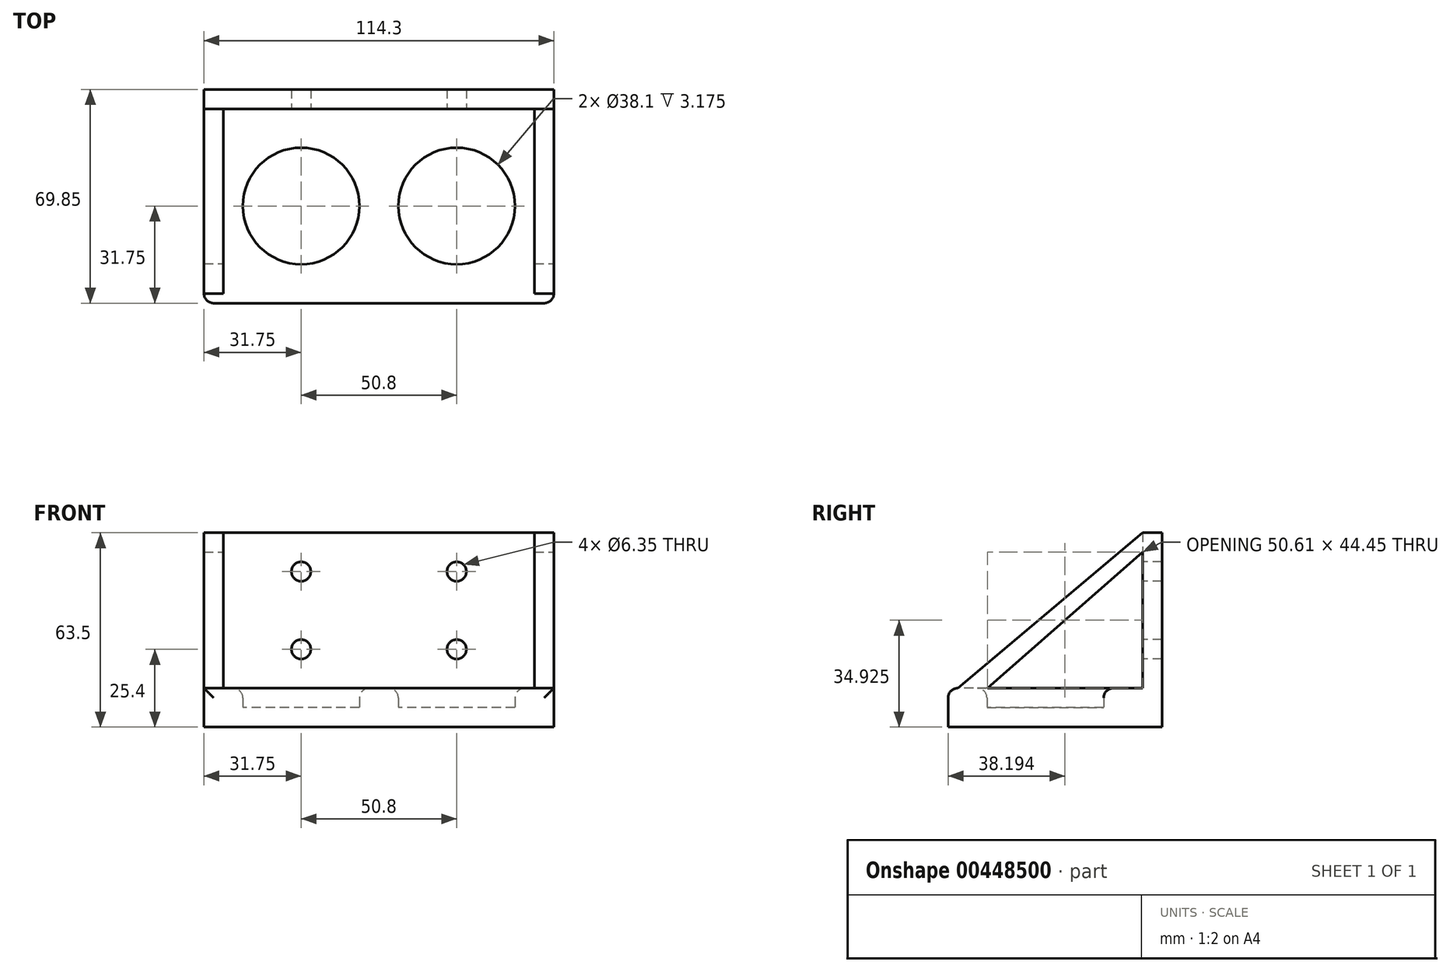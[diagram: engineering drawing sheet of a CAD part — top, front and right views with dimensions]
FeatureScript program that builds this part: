
annotation { "Feature Type Name" : "Feature", "Feature Type Description" : "" }
export const myFeature = defineFeature(function(context is Context, id is Id, definition is map)
    precondition{}
    {
        {
            var Q0;
            Q0=qCreatedBy(makeId("Top.planeOp"),FACE);
            var sketch = newSketch(context, id + "F0", { "sketchPlane" : qUnion([Q0])});
            skLineSegment(sketch, "E0.bottom", {"start": v(57.15, -31.75) * mm, "end": v(-57.15, -31.75) * mm});
            skLineSegment(sketch, "E0.top", {"start": v(57.15, 31.75) * mm, "end": v(-57.15, 31.75) * mm});
            skLineSegment(sketch, "E0.left", {"start": v(57.15, -31.75) * mm, "end": v(57.15, 31.75) * mm});
            skLineSegment(sketch, "E0.right", {"start": v(-57.15, -31.75) * mm, "end": v(-57.15, 31.75) * mm});
            skPoint(sketch, "E0.middle", {"position": v(0, 0) * mm});
            skCircle(sketch, "E1", {"center": v(-25.4, 0) * mm, "radius": 19.05 * mm});
            skCircle(sketch, "E2", {"center": v(25.4, 0) * mm, "radius": 19.05 * mm});
            skSolve(sketch);
        }
        {
            var Q0;
            Q0=makeQuery(id+"F0.imprint","IMPRINT",FACE,{"disambiguationData":[TD([[makeQuery(id+"F0.imprint","IMPRINT",EDGE,{"derivedFrom":sQuery(id+"F0.wireOp",EDGE,"E0.bottom")}),-1.0]])]});
            extrude(context, id + "F1", {"entities" : qUnion([Q0]), "depth" : 12.7 * mm});
        }
        {
            var Q0;
            Q0=makeQuery(id+"F0.imprint","IMPRINT",FACE,{"disambiguationData":[TD([[makeQuery(id+"F0.imprint","IMPRINT",EDGE,{"derivedFrom":sQuery(id+"F0.wireOp",EDGE,"E1")}),1.0]])]});
            var Q1;
            Q1=makeQuery(id+"F0.imprint","IMPRINT",FACE,{"disambiguationData":[TD([[makeQuery(id+"F0.imprint","IMPRINT",EDGE,{"derivedFrom":sQuery(id+"F0.wireOp",EDGE,"E2")}),1.0]])]});
            extrude(context, id + "F2", {"entities" : qUnion([Q0, Q1]), "operationType" : NewBodyOperationType.ADD, "depth" : 6.35 * mm});
        }
        {
            var Q0;
            Q0=makeQuery(id+"F1.opExtrude","CAP_FACE",FACE,{"disambiguationData":[OSD([sQuery(id+"F0.wireOp",EDGE,"E0.bottom"),sQuery(id+"F0.wireOp",EDGE,"E0.top"),sQuery(id+"F0.wireOp",EDGE,"E0.left"),sQuery(id+"F0.wireOp",EDGE,"E0.right"),sQuery(id+"F0.wireOp",EDGE,"E1"),sQuery(id+"F0.wireOp",EDGE,"E2")])],"isStart":false});
            var sketch = newSketch(context, id + "F3", { "sketchPlane" : qUnion([Q0])});
            skLineSegment(sketch, "E3", {"start": v(0, 31.75) * mm, "end": v(0, -28.58) * mm, "construction": true});
            skLineSegment(sketch, "E4.bottom", {"start": v(-57.15, 31.75) * mm, "end": v(-50.8, 31.75) * mm});
            skLineSegment(sketch, "E4.top", {"start": v(-57.15, -28.57) * mm, "end": v(-50.8, -28.57) * mm});
            skLineSegment(sketch, "E4.left", {"start": v(-57.15, 31.75) * mm, "end": v(-57.15, -28.58) * mm});
            skLineSegment(sketch, "E4.right", {"start": v(-50.8, 31.75) * mm, "end": v(-50.8, -28.57) * mm});
            skLineSegment(sketch, "E5.MirrorCS", {"start": v(50.8, 31.75) * mm, "end": v(50.8, -28.57) * mm});
            skLineSegment(sketch, "E6.MirrorCS", {"start": v(57.15, 31.75) * mm, "end": v(50.8, 31.75) * mm});
            skLineSegment(sketch, "E7.MirrorCS", {"start": v(57.15, -28.57) * mm, "end": v(50.8, -28.57) * mm});
            skLineSegment(sketch, "E8.MirrorCS", {"start": v(57.15, 31.75) * mm, "end": v(57.15, -28.58) * mm});
            skSolve(sketch);
        }
        {
            var Q0;
            Q0=makeQuery(id+"F3.imprint","IMPRINT",FACE,{"disambiguationData":[TD([[makeQuery(id+"F3.imprint","IMPRINT",EDGE,{"derivedFrom":sQuery(id+"F3.wireOp",EDGE,"E4.bottom")}),1.0]])]});
            var Q1;
            Q1=makeQuery(id+"F3.imprint","IMPRINT",FACE,{"disambiguationData":[TD([[makeQuery(id+"F3.imprint","IMPRINT",EDGE,{"derivedFrom":sQuery(id+"F3.wireOp",EDGE,"E5.MirrorCS")}),1.0]])]});
            extrude(context, id + "F4", {"entities" : qUnion([Q0, Q1]), "operationType" : NewBodyOperationType.ADD, "depth" : 50.8 * mm});
        }
        {
            var Q0;
            Q0=makeQuery(id+"F4.boolean.opBoolean","MERGE",FACE,{"derivedFrom":[makeQuery(id+"F1.opExtrude","SWEPT_FACE",FACE,{"disambiguationData":[OSD([sQuery(id+"F0.wireOp",EDGE,"E0.right")])]}),makeQuery(id+"F4.opExtrude","SWEPT_FACE",FACE,{"disambiguationData":[OSD([sQuery(id+"F3.wireOp",EDGE,"E4.left")])]})]});
            var sketch = newSketch(context, id + "F5", { "sketchPlane" : qUnion([Q0])});
            skLineSegment(sketch, "E9.0", {"start": v(-31.75, 12.7) * mm, "end": v(28.57, 12.7) * mm, "construction": true});
            skLineSegment(sketch, "E10", {"start": v(-31.75, 63.5) * mm, "end": v(28.58, 12.7) * mm});
            skSolve(sketch);
        }
        {
            var Q0;
            Q0=makeQuery(id+"F5.imprint","IMPRINT",FACE,{"disambiguationData":[TD([[makeQuery(id+"F5.imprint","IMPRINT",EDGE,{"derivedFrom":sQuery(id+"F5.wireOp",EDGE,"E10")}),1.0]])]});
            extrude(context, id + "F6", {"entities" : qUnion([Q0]), "operationType" : NewBodyOperationType.REMOVE, "endBound" : BoundingType.THROUGH_ALL, "oppositeDirection" : true, "depth" : 25.4 * mm});
        }
        {
            var Q0;
            Q0=makeQuery(id+"F4.boolean.opBoolean","MERGE",FACE,{"derivedFrom":[makeQuery(id+"F1.opExtrude","SWEPT_FACE",FACE,{"disambiguationData":[OSD([sQuery(id+"F0.wireOp",EDGE,"E0.top")])]}),makeQuery(id+"F4.opExtrude","SWEPT_FACE",FACE,{"disambiguationData":[OSD([sQuery(id+"F3.wireOp",EDGE,"E4.bottom")])]}),makeQuery(id+"F4.opExtrude","SWEPT_FACE",FACE,{"disambiguationData":[OSD([sQuery(id+"F3.wireOp",EDGE,"E6.MirrorCS")])]})]});
            var sketch = newSketch(context, id + "F7", { "sketchPlane" : qUnion([Q0])});
            skLineSegment(sketch, "E11.0", {"start": v(-50.8, 63.5) * mm, "end": v(-50.8, 12.7) * mm});
            skLineSegment(sketch, "E12.0", {"start": v(-50.8, 12.7) * mm, "end": v(50.8, 12.7) * mm});
            skLineSegment(sketch, "E13.0", {"start": v(50.8, 63.5) * mm, "end": v(50.8, 12.7) * mm});
            skLineSegment(sketch, "E14", {"start": v(-50.8, 63.5) * mm, "end": v(50.8, 63.5) * mm});
            skLineSegment(sketch, "E15", {"start": v(-50.8, 63.5) * mm, "end": v(50.8, 12.7) * mm, "construction": true});
            skLineSegment(sketch, "E16", {"start": v(50.8, 63.5) * mm, "end": v(-50.8, 12.7) * mm, "construction": true});
            skLineSegment(sketch, "E17", {"start": v(-50.8, 38.1) * mm, "end": v(50.8, 38.1) * mm, "construction": true});
            skLineSegment(sketch, "E18", {"start": v(50.8, 38.1) * mm, "end": v(0, 63.5) * mm, "construction": true});
            skLineSegment(sketch, "E19", {"start": v(0, 63.5) * mm, "end": v(0, 12.7) * mm, "construction": true});
            skLineSegment(sketch, "E20", {"start": v(0, 12.7) * mm, "end": v(-50.8, 38.1) * mm, "construction": true});
            skLineSegment(sketch, "E21", {"start": v(0, 63.5) * mm, "end": v(-50.8, 38.1) * mm, "construction": true});
            skLineSegment(sketch, "E22", {"start": v(50.8, 38.1) * mm, "end": v(0, 12.7) * mm, "construction": true});
            skCircle(sketch, "E23", {"center": v(-25.4, 50.8) * mm, "radius": 3.18 * mm});
            skCircle(sketch, "E24", {"center": v(25.4, 50.8) * mm, "radius": 3.18 * mm});
            skCircle(sketch, "E25", {"center": v(25.4, 25.4) * mm, "radius": 3.18 * mm});
            skCircle(sketch, "E26", {"center": v(-25.4, 25.4) * mm, "radius": 3.18 * mm});
            skSolve(sketch);
        }
        {
            var Q0;
            Q0=makeQuery(id+"F7.imprint","IMPRINT",FACE,{"disambiguationData":[TD([[makeQuery(id+"F7.imprint","IMPRINT",EDGE,{"derivedFrom":sQuery(id+"F7.wireOp",EDGE,"E11.0")}),-1.0]])]});
            var Q1;
            Q1=makeQuery(id+"F7.imprint","IMPRINT",FACE,{"disambiguationData":[TD([[makeQuery(id+"F7.imprint","IMPRINT",EDGE,{"derivedFrom":sQuery(id+"F7.wireOp",EDGE,"E11.0")}),1.0]])]});
            extrude(context, id + "F8", {"entities" : qUnion([Q0, Q1]), "operationType" : NewBodyOperationType.ADD, "depth" : 6.35 * mm});
        }
        {
            var Q0;
            Q0=makeQuery(id+"F1.opExtrude","CAP_EDGE",EDGE,{"disambiguationData":[OSD([sQuery(id+"F0.wireOp",EDGE,"E1")])],"isStart":false});
            var Q1;
            Q1=makeQuery(id+"F1.opExtrude","CAP_EDGE",EDGE,{"disambiguationData":[OSD([sQuery(id+"F0.wireOp",EDGE,"E2")])],"isStart":false});
            var Q2;
            Q2=makeQuery(id+"F1.opExtrude","CAP_EDGE",EDGE,{"disambiguationData":[OSD([sQuery(id+"F0.wireOp",EDGE,"E0.bottom")])],"isStart":false});
            var Q3;
            Q3=makeQuery(id+"F1.opExtrude","SWEPT_EDGE",EDGE,{"disambiguationData":[OSD([sQuery(id+"F0.wireOp",EDGE,"E0.bottom"),sQuery(id+"F0.wireOp",EDGE,"E0.left")])]});
            var Q4;
            Q4=makeQuery(id+"F1.opExtrude","SWEPT_EDGE",EDGE,{"disambiguationData":[OSD([sQuery(id+"F0.wireOp",EDGE,"E0.bottom"),sQuery(id+"F0.wireOp",EDGE,"E0.right")])]});
            fillet(context, id + "F9", {"entities" : qUnion([Q0, Q1, Q2, Q3, Q4]), "radius" : 3.17 * mm, "tangentPropagation" : true, "allowEdgeOverflow" : false});
        }
        {
            var Q0;
            {var subQ0=sQuery(id+"F3.wireOp",EDGE,"E8.MirrorCS");var subQ1=sQuery(id+"F0.wireOp",EDGE,"E0.left");Q0=makeQuery(id+"F8.boolean.opBoolean","MERGE",FACE,{"derivedFrom":[makeQuery(id+"F4.boolean.opBoolean","MERGE",FACE,{"derivedFrom":[makeQuery(id+"F1.opExtrude","SWEPT_FACE",FACE,{"disambiguationData":[OSD([subQ1])]}),makeQuery(id+"F4.opExtrude","SWEPT_FACE",FACE,{"disambiguationData":[OSD([subQ0])]})]}),makeQuery(id+"F8.opExtrude","SWEPT_FACE",FACE,{"disambiguationData":[OSD([sQuery(id+"F0.wireOp",EDGE,"E0.top"),subQ1,sQuery(id+"F3.wireOp",EDGE,"E6.MirrorCS"),subQ0])]})]});}
            var sketch = newSketch(context, id + "F10", { "sketchPlane" : qUnion([Q0])});
            skLineSegment(sketch, "E27.0", {"start": v(31.75, 63.5) * mm, "end": v(-28.58, 12.7) * mm});
            skLineSegment(sketch, "E28.0", {"start": v(38.1, 63.5) * mm, "end": v(38.1, 0) * mm});
            skLineSegment(sketch, "E29.0", {"start": v(-28.57, 0) * mm, "end": v(38.1, 0) * mm});
            skLineSegment(sketch, "E30.0", {"start": v(-28.57, 12.7) * mm, "end": v(-28.57, 0) * mm});
            skLineSegment(sketch, "E31", {"start": v(31.75, 57.15) * mm, "end": v(31.75, 12.7) * mm});
            skLineSegment(sketch, "E32", {"start": v(31.75, 12.7) * mm, "end": v(-22.22, 12.7) * mm});
            skLineSegment(sketch, "E33", {"start": v(-22.22, 9.75) * mm, "end": v(-22.22, 12.7) * mm});
            skLineSegment(sketch, "E34", {"start": v(-22.22, 9.75) * mm, "end": v(31.75, 57.15) * mm});
            skSolve(sketch);
        }
        {
            var Q0;
            Q0=makeQuery(id+"F10.imprint","IMPRINT",FACE,{"disambiguationData":[TD([[makeQuery(id+"F10.imprint","IMPRINT",EDGE,{"derivedFrom":sQuery(id+"F10.wireOp",EDGE,"E31")}),-1.0]])]});
            extrude(context, id + "F11", {"entities" : qUnion([Q0]), "operationType" : NewBodyOperationType.REMOVE, "endBound" : BoundingType.THROUGH_ALL, "oppositeDirection" : true, "depth" : 25.4 * mm});
        }
    });
